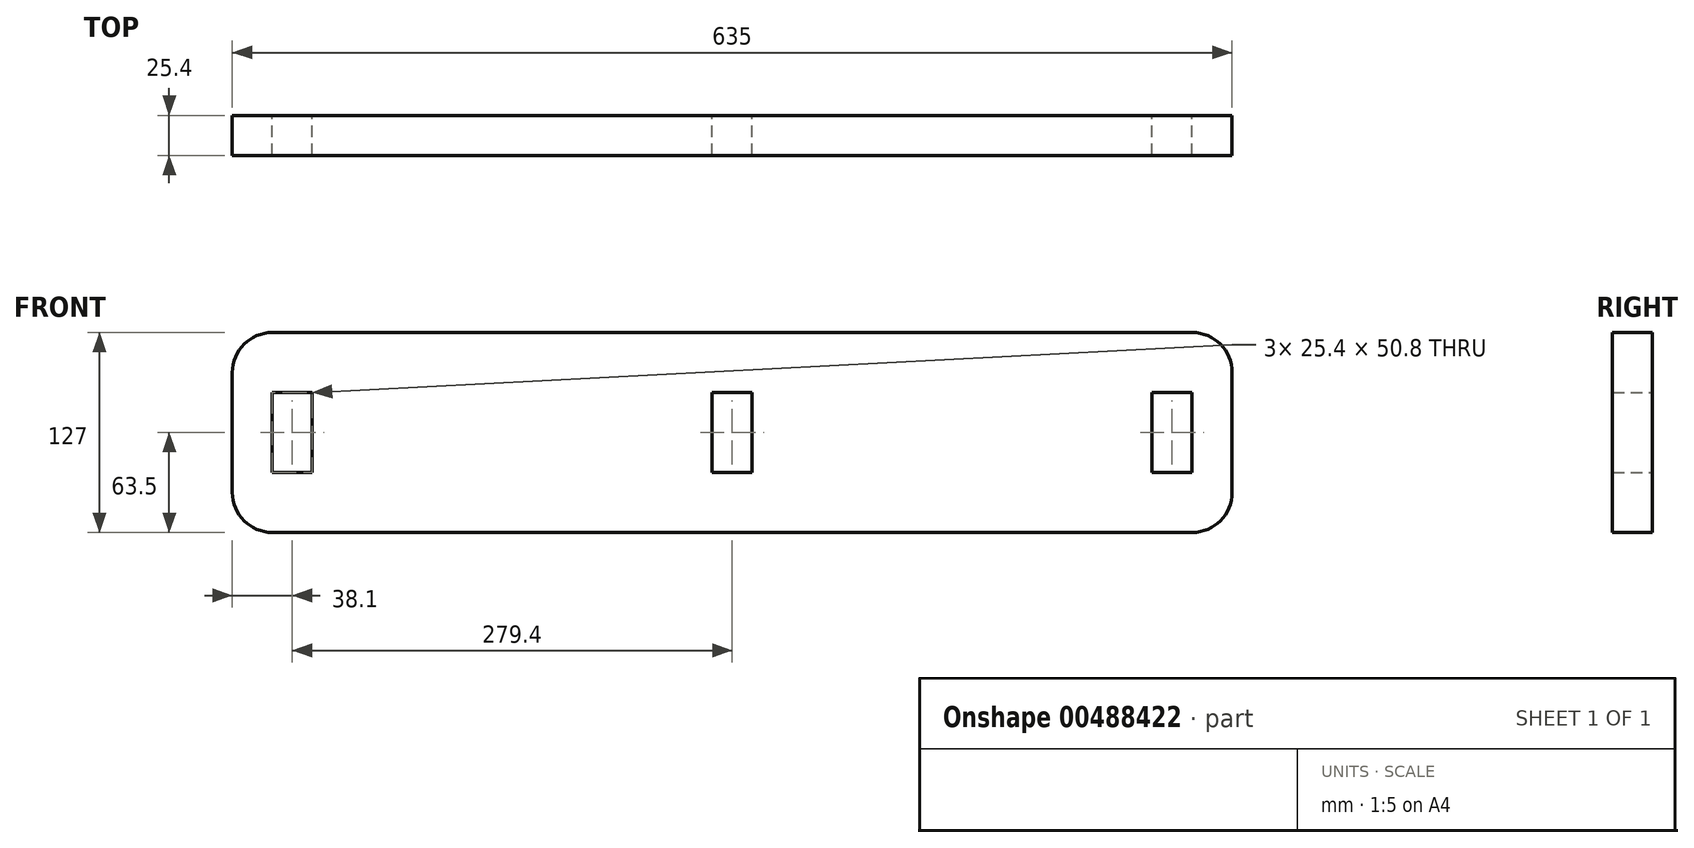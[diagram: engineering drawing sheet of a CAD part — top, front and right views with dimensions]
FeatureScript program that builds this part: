
annotation { "Feature Type Name" : "Feature", "Feature Type Description" : "" }
export const myFeature = defineFeature(function(context is Context, id is Id, definition is map)
    precondition{}
    {
        {
            var Q0;
            Q0=qCreatedBy(makeId("Right.planeOp"),FACE);
            var sketch = newSketch(context, id + "F0", { "sketchPlane" : qUnion([Q0])});
            skLineSegment(sketch, "E0.bottom", {"start": v(12.7, 63.5) * mm, "end": v(-12.7, 63.5) * mm});
            skLineSegment(sketch, "E0.top", {"start": v(12.7, -63.5) * mm, "end": v(-12.7, -63.5) * mm});
            skLineSegment(sketch, "E0.left", {"start": v(12.7, 63.5) * mm, "end": v(12.7, -63.5) * mm});
            skLineSegment(sketch, "E0.right", {"start": v(-12.7, 63.5) * mm, "end": v(-12.7, -63.5) * mm});
            skPoint(sketch, "E0.middle", {"position": v(0, 0) * mm});
            skSolve(sketch);
        }
        {
            var Q0;
            Q0 = qSketchRegion(id + "F0", true);
            extrude(context, id + "F1", {"entities" : qUnion([Q0]), "flatOperationType" : FlatOperationType.REMOVE, "depth" : 635 * mm, "offsetDistance" : 25.4 * mm, "domain" : OperationDomain.MODEL, "symmetric" : true});
        }
        {
            var Q0;
            Q0=makeQuery(id+"F1.opExtrude","SWEPT_FACE",FACE,{"disambiguationData":[OSD([sQuery(id+"F0.wireOp",EDGE,"E0.left")])]});
            var sketch = newSketch(context, id + "F2", { "sketchPlane" : qUnion([Q0])});
            skLineSegment(sketch, "E1.bottom", {"start": v(-292.1, 25.4) * mm, "end": v(-266.7, 25.4) * mm});
            skLineSegment(sketch, "E1.top", {"start": v(-292.1, -25.4) * mm, "end": v(-266.7, -25.4) * mm});
            skLineSegment(sketch, "E1.left", {"start": v(-292.1, 25.4) * mm, "end": v(-292.1, -25.4) * mm});
            skLineSegment(sketch, "E1.right", {"start": v(-266.7, 25.4) * mm, "end": v(-266.7, -25.4) * mm});
            skLineSegment(sketch, "E2.bottom", {"start": v(266.7, 25.4) * mm, "end": v(292.1, 25.4) * mm});
            skLineSegment(sketch, "E2.top", {"start": v(266.7, -25.4) * mm, "end": v(292.1, -25.4) * mm});
            skLineSegment(sketch, "E2.left", {"start": v(266.7, 25.4) * mm, "end": v(266.7, -25.4) * mm});
            skLineSegment(sketch, "E2.right", {"start": v(292.1, 25.4) * mm, "end": v(292.1, -25.4) * mm});
            skLineSegment(sketch, "E3.bottom", {"start": v(-12.7, 25.4) * mm, "end": v(12.7, 25.4) * mm});
            skLineSegment(sketch, "E3.top", {"start": v(-12.7, -25.4) * mm, "end": v(12.7, -25.4) * mm});
            skLineSegment(sketch, "E3.left", {"start": v(-12.7, 25.4) * mm, "end": v(-12.7, -25.4) * mm});
            skLineSegment(sketch, "E3.right", {"start": v(12.7, 25.4) * mm, "end": v(12.7, -25.4) * mm});
            skPoint(sketch, "E3.middle", {"position": v(0, 0) * mm});
            skSolve(sketch);
        }
        {
            var Q0;
            Q0 = qSketchRegion(id + "F2", true);
            var Q1;
            Q1=makeQuery(id+"F1.opExtrude","SWEPT_FACE",FACE,{"disambiguationData":[OSD([sQuery(id+"F0.wireOp",EDGE,"E0.right")])]});
            extrude(context, id + "F3", {"entities" : qUnion([Q0]), "operationType" : NewBodyOperationType.REMOVE, "endBound" : BoundingType.UP_TO_SURFACE, "oppositeDirection" : true, "depth" : 25.4 * mm, "endBoundEntityFace" : qUnion([Q1]), "offsetDistance" : 25.4 * mm});
        }
        {
            var Q0;
            Q0=makeQuery(id+"F1.opExtrude","CAP_EDGE",EDGE,{"disambiguationData":[OSD([sQuery(id+"F0.wireOp",EDGE,"E0.bottom")])],"isStart":true});
            var Q1;
            Q1=makeQuery(id+"F1.opExtrude","CAP_EDGE",EDGE,{"disambiguationData":[OSD([sQuery(id+"F0.wireOp",EDGE,"E0.top")])],"isStart":true});
            var Q2;
            Q2=makeQuery(id+"F1.opExtrude","CAP_EDGE",EDGE,{"disambiguationData":[OSD([sQuery(id+"F0.wireOp",EDGE,"E0.bottom")])],"isStart":false});
            var Q3;
            Q3=makeQuery(id+"F1.opExtrude","CAP_EDGE",EDGE,{"disambiguationData":[OSD([sQuery(id+"F0.wireOp",EDGE,"E0.top")])],"isStart":false});
            fillet(context, id + "F4", {"entities" : qUnion([Q0, Q1, Q2, Q3]), "tangentPropagation" : true, "radius" : 25.4 * mm, "defaultsChanged" : true, "vertexSettings" : [], "allowEdgeOverflow" : false});
        }
    });
